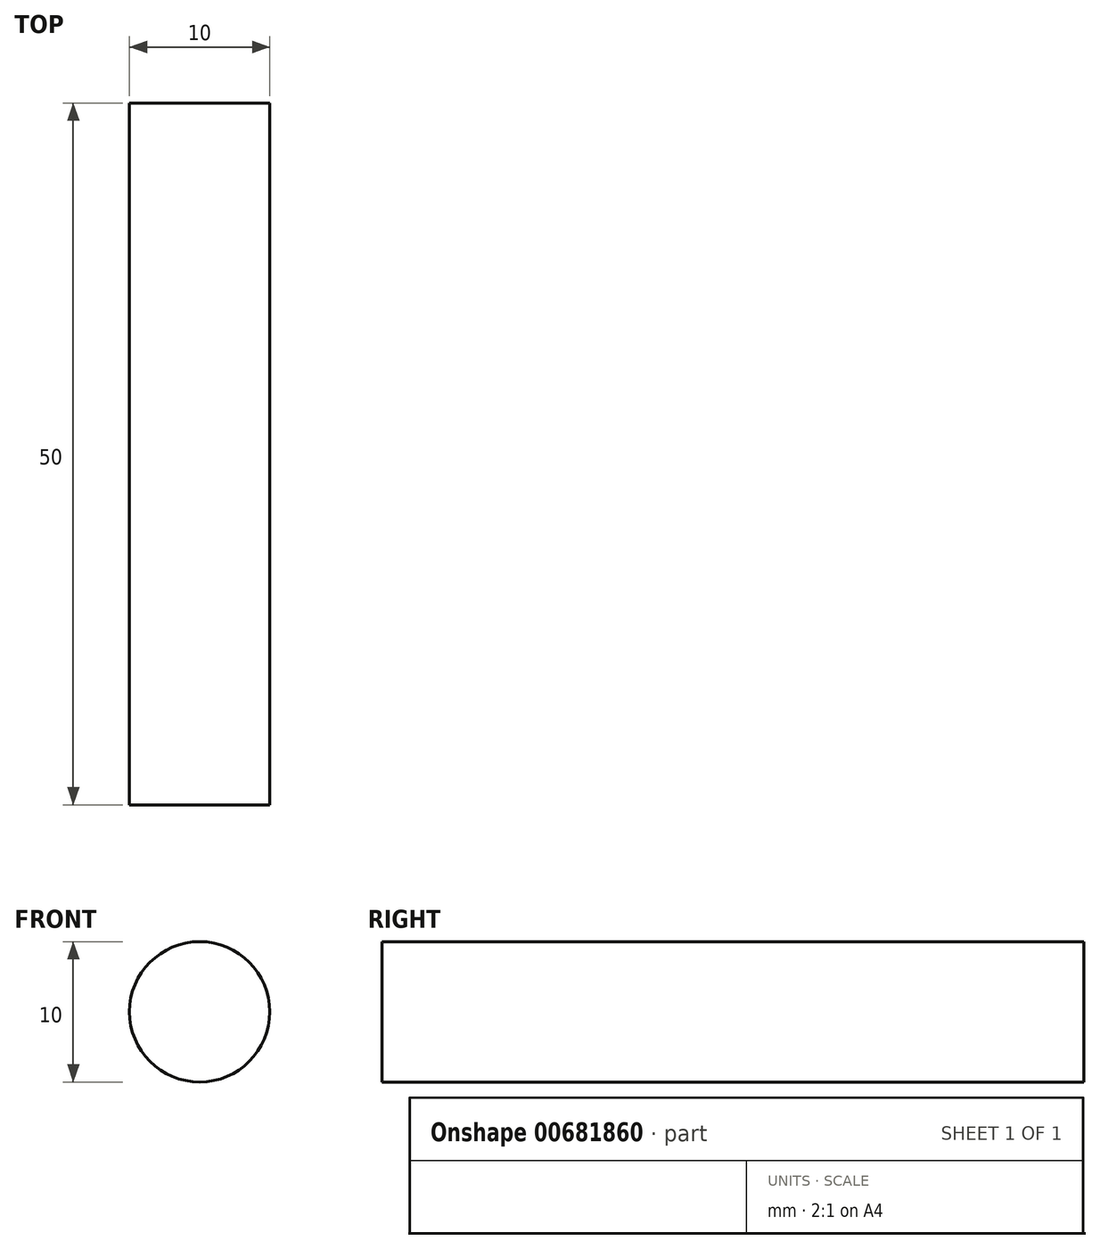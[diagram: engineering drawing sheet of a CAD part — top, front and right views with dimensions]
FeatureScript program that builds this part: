
annotation { "Feature Type Name" : "Feature", "Feature Type Description" : "" }
export const myFeature = defineFeature(function(context is Context, id is Id, definition is map)
    precondition{}
    {
        {
            var Q0;
            Q0=qCreatedBy(makeId("Front.planeOp"),FACE);
            var sketch = newSketch(context, id + "F0", { "sketchPlane" : qUnion([Q0])});
            skCircle(sketch, "E0", {"center": v(0, 0) * mm, "radius": 5 * mm});
            skSolve(sketch);
        }
        {
            var Q0;
            Q0 = qSketchRegion(id + "F0", true);
            extrude(context, id + "F1", {"entities" : qUnion([Q0]), "endBound" : BoundingType.SYMMETRIC, "depth" : 50 * mm, "offsetDistance" : 25 * mm});
        }
    });
